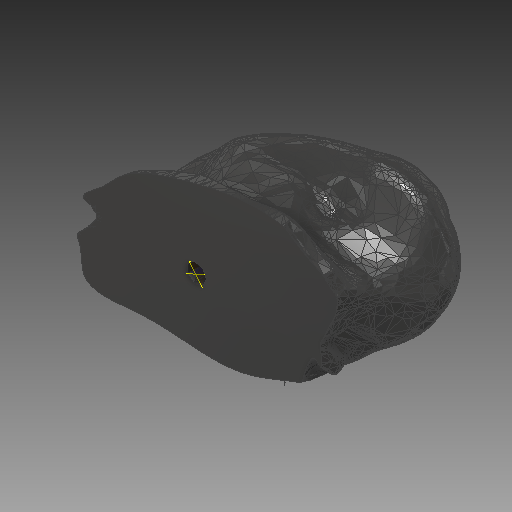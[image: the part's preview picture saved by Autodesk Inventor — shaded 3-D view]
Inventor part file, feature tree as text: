
AUTODESK INVENTOR PART (.ipt)
format: ipt  version: 2019 (Build 230136000, 136)  size: 10,624,512 bytes
history: native  units: in
note: dims shown in document units (in); Inventor stores cm internally (conversion verified against a paired STEP export)
features: other x4, plane x2
ambient origin geometry x8: Origin, YZ Plane, XZ Plane, XY Plane, X Axis, Y Axis, Z Axis, Center Point
bodies: Solid1 (feature_tree)
feature tree (6):
  other  "ear_right_cut.ipt"
  other  "Solid1::ear_right_cut.ipt"
  other  "TaggingFeature1"
  plane  "Work Plane1"
  plane  "Work Plane2"
  other  "Work Axis1"
